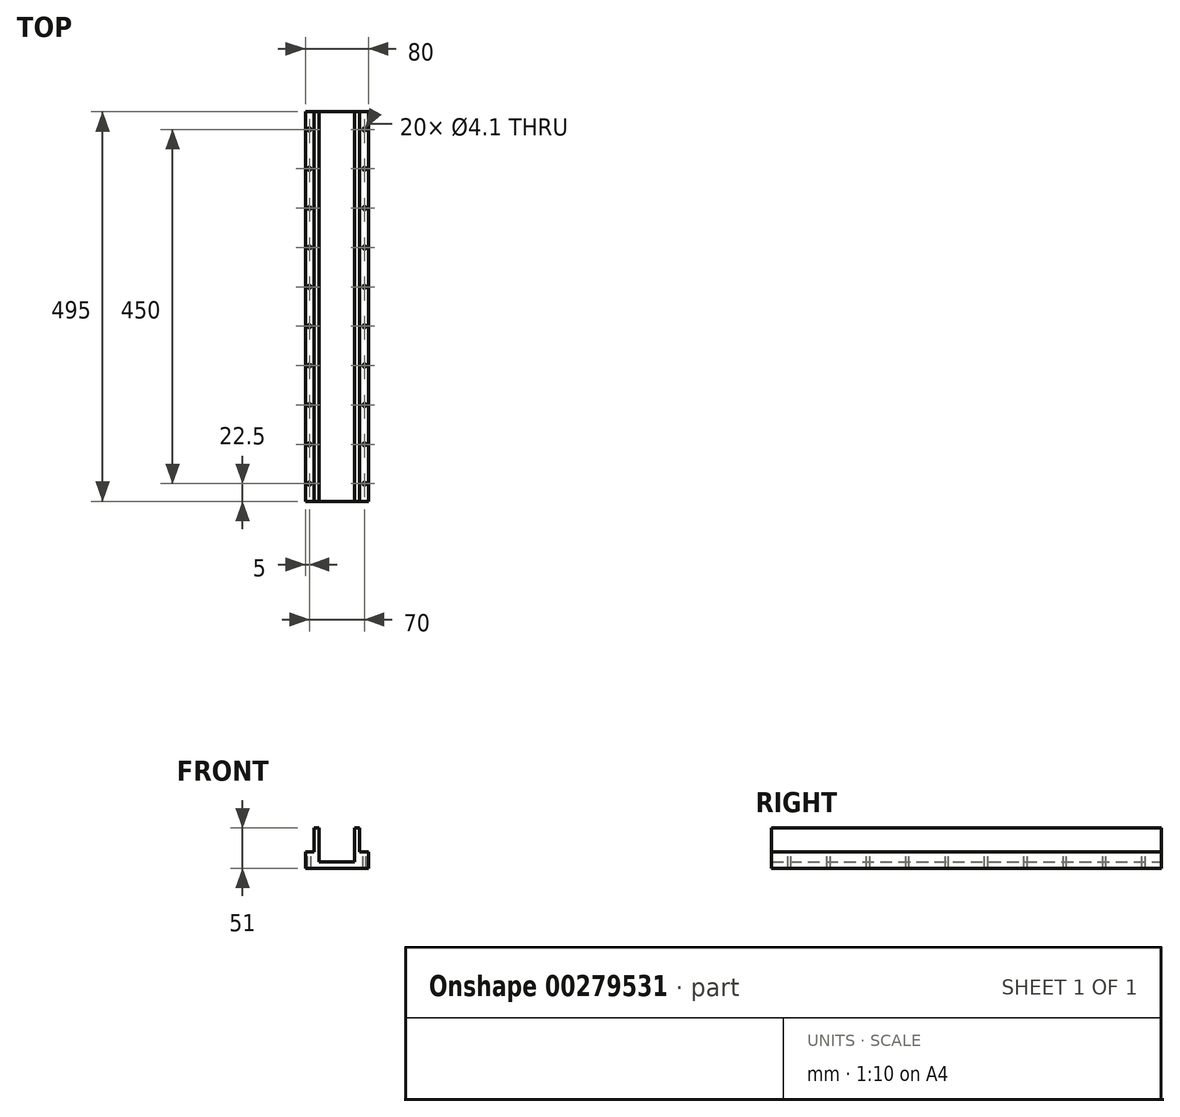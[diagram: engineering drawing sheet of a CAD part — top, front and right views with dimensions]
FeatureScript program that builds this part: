
annotation { "Feature Type Name" : "Feature", "Feature Type Description" : "" }
export const myFeature = defineFeature(function(context is Context, id is Id, definition is map)
    precondition{}
    {
        {
            var Q0;
            Q0=qCreatedBy(makeId("Front.planeOp"),FACE);
            var sketch = newSketch(context, id + "F0", { "sketchPlane" : qUnion([Q0])});
            skLineSegment(sketch, "E0.bottom", {"start": v(0, 0) * mm, "end": v(80, 0) * mm});
            skLineSegment(sketch, "E0.top", {"start": v(0, 21) * mm, "end": v(80, 21) * mm});
            skLineSegment(sketch, "E0.left", {"start": v(0, 0) * mm, "end": v(0, 21) * mm});
            skLineSegment(sketch, "E0.right", {"start": v(80, 0) * mm, "end": v(80, 21) * mm});
            skLineSegment(sketch, "E1.bottom", {"start": v(11, 21) * mm, "end": v(69, 21) * mm});
            skLineSegment(sketch, "E1.top", {"start": v(11, 51) * mm, "end": v(69, 51) * mm});
            skLineSegment(sketch, "E1.left", {"start": v(11, 21) * mm, "end": v(11, 51) * mm});
            skLineSegment(sketch, "E1.right", {"start": v(69, 21) * mm, "end": v(69, 51) * mm});
            skLineSegment(sketch, "E2.bottom", {"start": v(17.5, 51) * mm, "end": v(62.5, 51) * mm});
            skLineSegment(sketch, "E2.top", {"start": v(17.5, 8) * mm, "end": v(62.5, 8) * mm});
            skLineSegment(sketch, "E2.left", {"start": v(17.5, 51) * mm, "end": v(17.5, 8) * mm});
            skLineSegment(sketch, "E2.right", {"start": v(62.5, 51) * mm, "end": v(62.5, 8) * mm});
            skSolve(sketch);
        }
        {
            var Q0;
            {var subQ0=sQuery(id+"F0.wireOp",EDGE,"E1.left");Q0=makeQuery(id+"F0.imprint","IMPRINT",FACE,{"disambiguationData":[TD([[makeQuery(id+"F0.imprint","IMPRINT",EDGE,{"derivedFrom":subQ0}),-1.0]])]});}
            var Q1;
            {var subQ0=sQuery(id+"F0.wireOp",EDGE,"E1.right");Q1=makeQuery(id+"F0.imprint","IMPRINT",FACE,{"disambiguationData":[TD([[makeQuery(id+"F0.imprint","IMPRINT",EDGE,{"derivedFrom":subQ0}),1.0]])]});}
            var Q2;
            Q2=makeQuery(id+"F0.imprint","IMPRINT",FACE,{"disambiguationData":[TD([[makeQuery(id+"F0.imprint","IMPRINT",EDGE,{"derivedFrom":sQuery(id+"F0.wireOp",EDGE,"E0.bottom")}),1.0]])]});
            extrude(context, id + "F1", {"entities" : qUnion([Q0, Q1, Q2]), "depth" : 495 * mm});
        }
        {
            var Q0;
            {var subQ0=sQuery(id+"F0.wireOp",EDGE,"E0.top");Q0=makeQuery(id+"F1.opExtrude","SWEPT_FACE",FACE,{"disambiguationData":[OSD([subQ0]),TDD([makeQuery(id+"F0.imprint","IMPRINT",EDGE,{"disambiguationData":[TD([[makeQuery(id+"F0.imprint","INTERSECT",VERTEX,{"derivedFrom":[subQ0,sQuery(id+"F0.wireOp",EDGE,"E0.right")]}),1.0]])],"derivedFrom":subQ0})])]});}
            var sketch = newSketch(context, id + "F2", { "sketchPlane" : qUnion([Q0])});
            skPoint(sketch, "E3", {"position": v(5, -22.5) * mm});
            skPoint(sketch, "E4.0.1.0", {"position": v(5, -72.5) * mm});
            skPoint(sketch, "E4.0.2.0", {"position": v(5, -122.5) * mm});
            skPoint(sketch, "E4.0.3.0", {"position": v(5, -172.5) * mm});
            skPoint(sketch, "E4.0.4.0", {"position": v(5, -222.5) * mm});
            skPoint(sketch, "E4.0.5.0", {"position": v(5, -272.5) * mm});
            skPoint(sketch, "E4.0.6.0", {"position": v(5, -322.5) * mm});
            skPoint(sketch, "E4.0.7.0", {"position": v(5, -372.5) * mm});
            skPoint(sketch, "E4.0.8.0", {"position": v(5, -422.5) * mm});
            skPoint(sketch, "E4.0.9.0", {"position": v(5, -472.5) * mm});
            skPoint(sketch, "E4.1.0.0", {"position": v(75, -22.5) * mm});
            skPoint(sketch, "E4.1.1.0", {"position": v(75, -72.5) * mm});
            skPoint(sketch, "E4.1.2.0", {"position": v(75, -122.5) * mm});
            skPoint(sketch, "E4.1.3.0", {"position": v(75, -172.5) * mm});
            skPoint(sketch, "E4.1.4.0", {"position": v(75, -222.5) * mm});
            skPoint(sketch, "E4.1.5.0", {"position": v(75, -272.5) * mm});
            skPoint(sketch, "E4.1.6.0", {"position": v(75, -322.5) * mm});
            skPoint(sketch, "E4.1.7.0", {"position": v(75, -372.5) * mm});
            skPoint(sketch, "E4.1.8.0", {"position": v(75, -422.5) * mm});
            skPoint(sketch, "E4.1.9.0", {"position": v(75, -472.5) * mm});
            skLineSegment(sketch, "E4.direction1", {"start": v(5, -22.5) * mm, "end": v(75, -22.5) * mm, "construction": true});
            skLineSegment(sketch, "E4.direction2", {"start": v(5, -22.5) * mm, "end": v(5, -72.5) * mm, "construction": true});
            skSolve(sketch);
        }
        {
            var Q0;
            Q0=sQuery(id+"F2.wireOp",VERTEX,"E4.1.0.0");
            var Q1;
            Q1=sQuery(id+"F2.wireOp",VERTEX,"E4.1.1.0");
            var Q2;
            Q2=sQuery(id+"F2.wireOp",VERTEX,"E4.1.2.0");
            var Q3;
            Q3=sQuery(id+"F2.wireOp",VERTEX,"E4.1.3.0");
            var Q4;
            Q4=sQuery(id+"F2.wireOp",VERTEX,"E4.1.4.0");
            var Q5;
            Q5=sQuery(id+"F2.wireOp",VERTEX,"E4.1.5.0");
            var Q6;
            Q6=sQuery(id+"F2.wireOp",VERTEX,"E4.1.6.0");
            var Q7;
            Q7=sQuery(id+"F2.wireOp",VERTEX,"E4.1.7.0");
            var Q8;
            Q8=sQuery(id+"F2.wireOp",VERTEX,"E4.1.8.0");
            var Q9;
            Q9=sQuery(id+"F2.wireOp",VERTEX,"E4.1.9.0");
            var Q10;
            Q10=sQuery(id+"F2.wireOp",VERTEX,"E3");
            var Q11;
            Q11=sQuery(id+"F2.wireOp",VERTEX,"E4.0.1.0");
            var Q12;
            Q12=sQuery(id+"F2.wireOp",VERTEX,"E4.0.2.0");
            var Q13;
            Q13=sQuery(id+"F2.wireOp",VERTEX,"E4.0.3.0");
            var Q14;
            Q14=sQuery(id+"F2.wireOp",VERTEX,"E4.0.4.0");
            var Q15;
            Q15=sQuery(id+"F2.wireOp",VERTEX,"E4.0.5.0");
            var Q16;
            Q16=sQuery(id+"F2.wireOp",VERTEX,"E4.0.6.0");
            var Q17;
            Q17=sQuery(id+"F2.wireOp",VERTEX,"E4.0.7.0");
            var Q18;
            Q18=sQuery(id+"F2.wireOp",VERTEX,"E4.0.8.0");
            var Q19;
            Q19=sQuery(id+"F2.wireOp",VERTEX,"E4.0.9.0");
            var Q20;
            Q20=makeQuery(id+"F1.opExtrude","SWEPT_BODY",BODY,{"disambiguationData":[OSD([sQuery(id+"F0.wireOp",EDGE,"E0.bottom"),sQuery(id+"F0.wireOp",EDGE,"E0.top"),sQuery(id+"F0.wireOp",EDGE,"E0.left"),sQuery(id+"F0.wireOp",EDGE,"E0.right"),sQuery(id+"F0.wireOp",EDGE,"E1.top"),sQuery(id+"F0.wireOp",EDGE,"E1.left"),sQuery(id+"F0.wireOp",EDGE,"E1.right"),sQuery(id+"F0.wireOp",EDGE,"E2.top"),sQuery(id+"F0.wireOp",EDGE,"E2.left"),sQuery(id+"F0.wireOp",EDGE,"E2.right")])]});
            hole(context, id + "F3", {"style" : HoleStyle.SIMPLE, "endStyle" : HoleEndStyle.THROUGH, "holeDiameter" : 4.1 * mm, "tappedDepth" : 12 * mm, "tapClearance" : 3, "locations" : qUnion([Q0, Q1, Q2, Q3, Q4, Q5, Q6, Q7, Q8, Q9, Q10, Q11, Q12, Q13, Q14, Q15, Q16, Q17, Q18, Q19]), "scope" : qUnion([Q20])});
        }
    });
